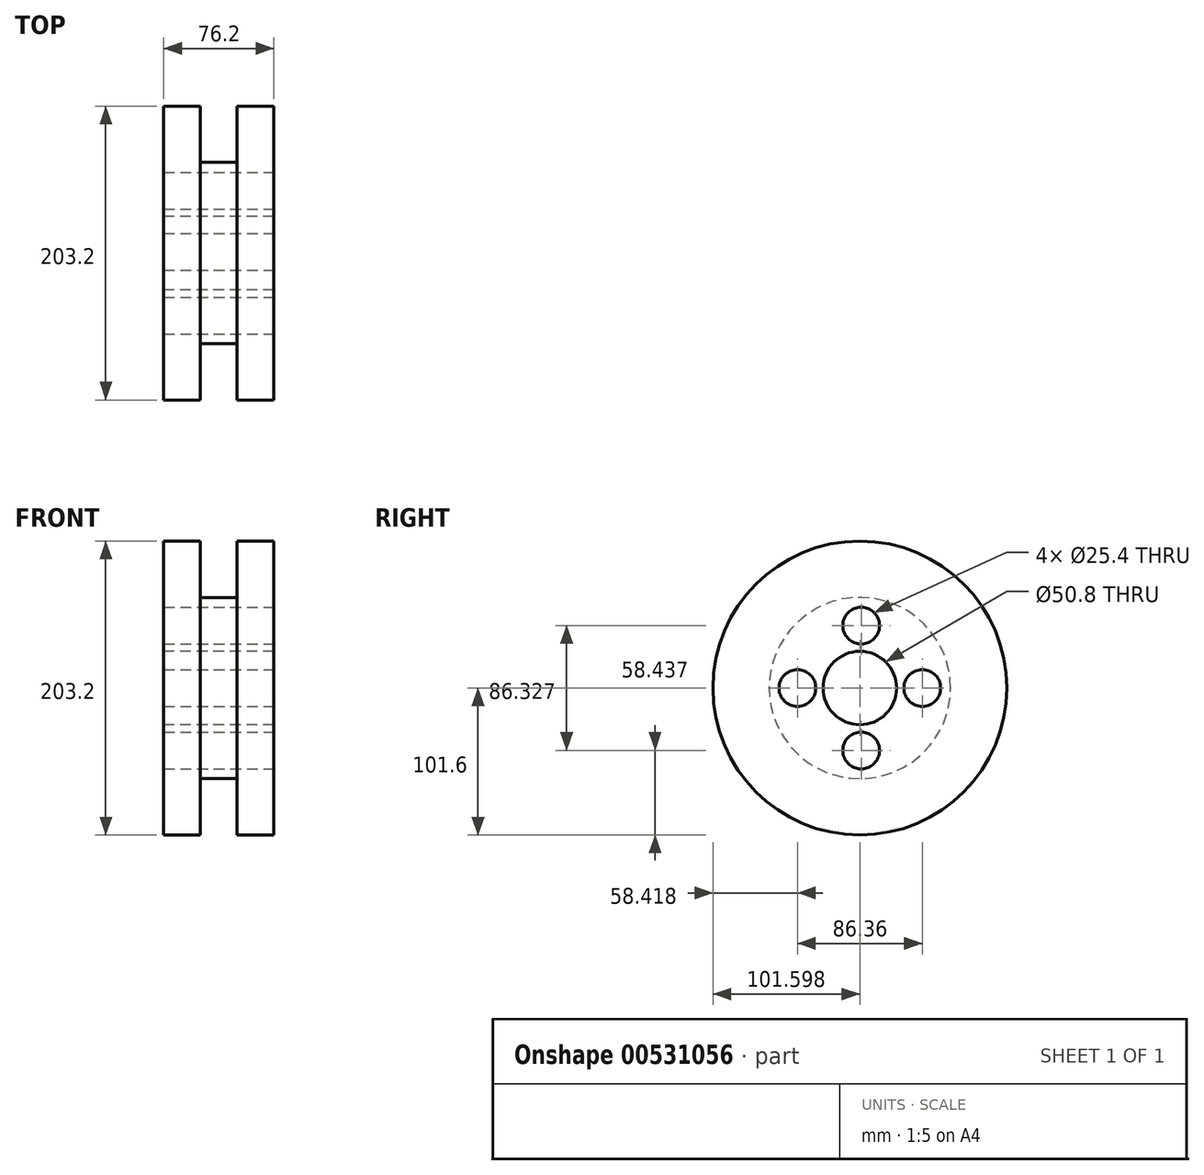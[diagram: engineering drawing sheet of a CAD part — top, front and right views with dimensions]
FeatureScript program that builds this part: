
annotation { "Feature Type Name" : "Feature", "Feature Type Description" : "" }
export const myFeature = defineFeature(function(context is Context, id is Id, definition is map)
    precondition{}
    {
        {
            var Q0;
            Q0=qCreatedBy(makeId("Top.planeOp"),FACE);
            var sketch = newSketch(context, id + "F0", { "sketchPlane" : qUnion([Q0])});
            skLineSegment(sketch, "E0", {"start": v(-25.4, 38.93) * mm, "end": v(0, 38.93) * mm});
            skLineSegment(sketch, "E1", {"start": v(0, 38.93) * mm, "end": v(0, 0) * mm});
            skLineSegment(sketch, "E2", {"start": v(0, 0) * mm, "end": v(25.4, 0) * mm});
            skLineSegment(sketch, "E3", {"start": v(25.4, 0) * mm, "end": v(25.4, 38.93) * mm});
            skLineSegment(sketch, "E4", {"start": v(25.4, 38.93) * mm, "end": v(50.8, 38.93) * mm});
            skLineSegment(sketch, "E5", {"start": v(50.8, 38.93) * mm, "end": v(50.8, -37.27) * mm});
            skLineSegment(sketch, "E6", {"start": v(50.8, -37.27) * mm, "end": v(-25.4, -37.27) * mm});
            skLineSegment(sketch, "E7", {"start": v(-25.4, -37.27) * mm, "end": v(-25.4, 38.93) * mm});
            skLineSegment(sketch, "E8", {"start": v(-25.4, -37.27) * mm, "end": v(-25.4, -62.67) * mm});
            skLineSegment(sketch, "E9", {"start": v(-25.4, -62.67) * mm, "end": v(50.8, -62.67) * mm});
            skSolve(sketch);
        }
        {
            var Q0;
            Q0 = qSketchRegion(id + "F0", true);
            var Q1;
            Q1=sQuery(id+"F0.wireOp",EDGE,"E9");
            revolve(context, id + "F1", {"entities" : qUnion([Q0]), "axis" : qUnion([Q1]), "revolveType" : RevolveType.FULL});
        }
        {
            var Q0;
            Q0=makeQuery(id+"F1.opRevolve","SWEPT_FACE",FACE,{"disambiguationData":[OSD([sQuery(id+"F0.wireOp",EDGE,"E5")])]});
            var sketch = newSketch(context, id + "F2", { "sketchPlane" : qUnion([Q0])});
            skLineSegment(sketch, "E10", {"start": v(-61.75, -25.38) * mm, "end": v(-61.75, -43.16) * mm});
            skLineSegment(sketch, "E11", {"start": v(-61.75, 25.38) * mm, "end": v(-61.75, 43.16) * mm});
            skLineSegment(sketch, "E12", {"start": v(-37.27, 0) * mm, "end": v(-19.5, 0) * mm});
            skLineSegment(sketch, "E13", {"start": v(-88.07, 0) * mm, "end": v(-105.85, 0) * mm});
            skCircle(sketch, "E14", {"center": v(-19.5, 0) * mm, "radius": 12.7 * mm});
            skCircle(sketch, "E15", {"center": v(-61.75, -43.16) * mm, "radius": 12.7 * mm});
            skCircle(sketch, "E16", {"center": v(-105.85, 0) * mm, "radius": 12.7 * mm});
            skCircle(sketch, "E17", {"center": v(-61.75, 43.16) * mm, "radius": 12.7 * mm});
            skSolve(sketch);
        }
        {
            var Q0;
            Q0 = qSketchRegion(id + "F2", true);
            extrude(context, id + "F3", {"entities" : qUnion([Q0]), "operationType" : NewBodyOperationType.REMOVE, "endBound" : BoundingType.UP_TO_NEXT, "oppositeDirection" : true, "depth" : 76.2 * mm, "offsetDistance" : 25.4 * mm});
        }
    });
